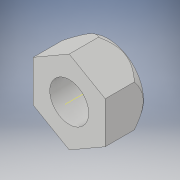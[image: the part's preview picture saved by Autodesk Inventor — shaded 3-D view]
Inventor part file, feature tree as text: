
AUTODESK INVENTOR PART (.ipt)
format: ipt  version: 2018 (Build 220112000, 112)  size: 119,808 bytes
history: native  units: in
note: dims shown in document units (in); Inventor stores cm internally (conversion verified against a paired STEP export)
features: sketch x2, extrude x1, other x1, revolve x1
ambient origin geometry x8: Origin, YZ Plane, XZ Plane, XY Plane, X Axis, Y Axis, Z Axis, Center Point
bodies: Solid1 (feature_tree)
feature tree (5):
  extrude  "Extrusion1"  Depth=0.4724in TaperAngle=0.0deg
  other  "Work Axis1"
  revolve  "Revolution1"  [1 undecoded]
  sketch  "Sketch2"  dims[d0=0.4724in d1=0.4724in d2=0.0in]
  sketch  "Sketch5"  dims[d3=90.0deg]
note: 1 required parameter value undecoded (feature->parameter linkage not recoverable at this tier; creation-order binding heuristic only, values carry confidence <= 0.55)
